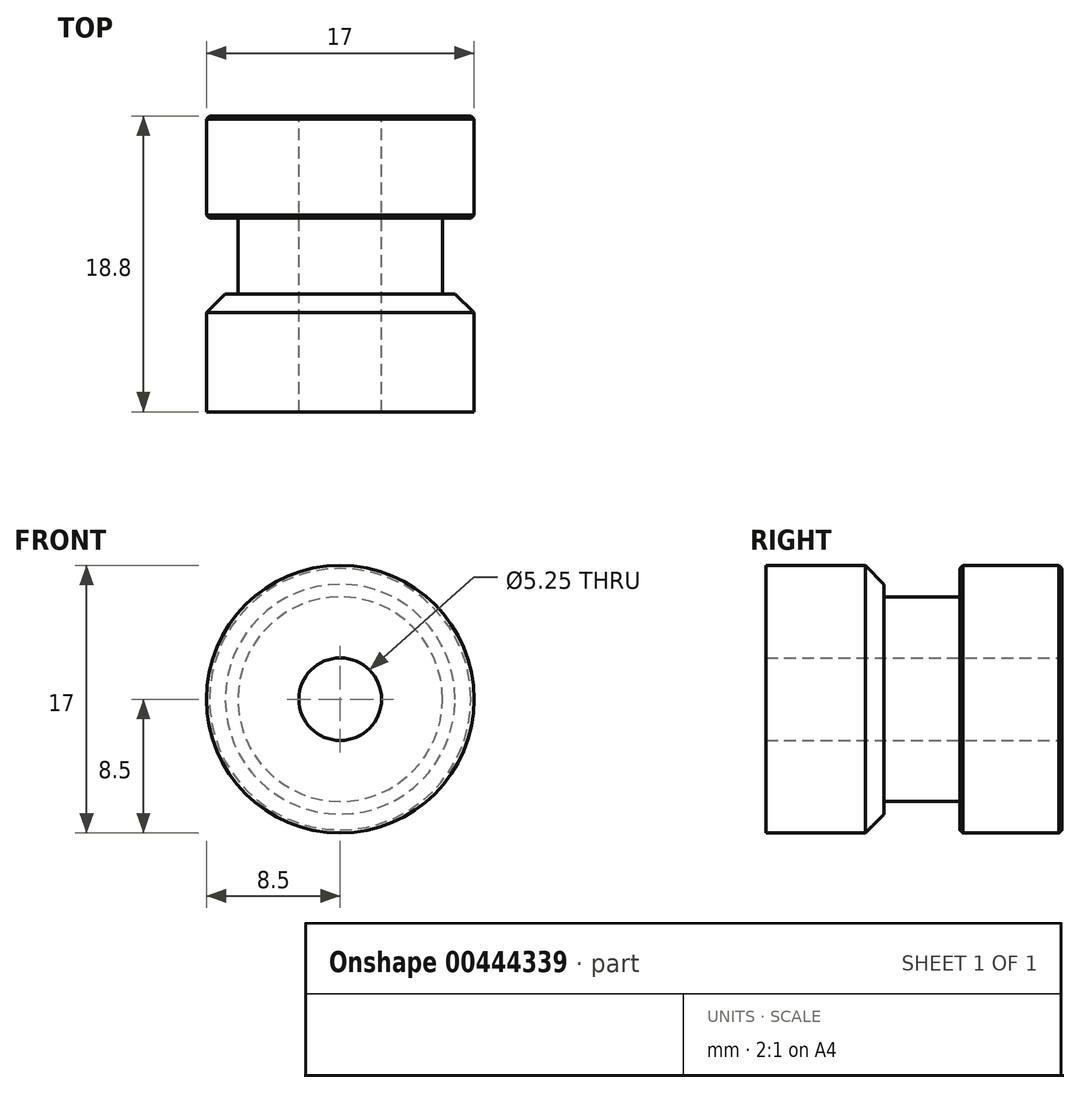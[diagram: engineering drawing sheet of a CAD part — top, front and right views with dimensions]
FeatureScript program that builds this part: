
annotation { "Feature Type Name" : "Feature", "Feature Type Description" : "" }
export const myFeature = defineFeature(function(context is Context, id is Id, definition is map)
    precondition{}
    {
        {
            var Q0;
            Q0=qCreatedBy(makeId("Front.planeOp"),FACE);
            var sketch = newSketch(context, id + "F0", { "sketchPlane" : qUnion([Q0])});
            skCircle(sketch, "E0", {"center": v(0, 0) * mm, "radius": 8.5 * mm});
            skCircle(sketch, "E1", {"center": v(0, 0) * mm, "radius": 2.63 * mm});
            skSolve(sketch);
        }
        {
            var Q0;
            Q0=makeQuery(id+"F0.imprint","IMPRINT",FACE,{"disambiguationData":[TD([[makeQuery(id+"F0.imprint","IMPRINT",EDGE,{"derivedFrom":sQuery(id+"F0.wireOp",EDGE,"E0")}),1.0]])]});
            extrude(context, id + "F1", {"entities" : qUnion([Q0]), "depth" : 6.5 * mm});
        }
        {
            var Q0;
            Q0=makeQuery(id+"F1.opExtrude","CAP_EDGE",EDGE,{"disambiguationData":[OSD([sQuery(id+"F0.wireOp",EDGE,"E0")])],"isStart":true});
            chamfer(context, id + "F2", {"entities" : qUnion([Q0]), "width" : 0.2 * mm, "tangentPropagation" : true});
        }
        {
            var Q0;
            Q0=makeQuery(id+"F1.opExtrude","CAP_FACE",FACE,{"disambiguationData":[OSD([sQuery(id+"F0.wireOp",EDGE,"E0"),sQuery(id+"F0.wireOp",EDGE,"E1")])],"isStart":false});
            var sketch = newSketch(context, id + "F3", { "sketchPlane" : qUnion([Q0])});
            skCircle(sketch, "E2", {"center": v(0, 0) * mm, "radius": 6.5 * mm});
            skCircle(sketch, "E3", {"center": v(0, 0) * mm, "radius": 2.62 * mm});
            skSolve(sketch);
        }
        {
            var Q0;
            Q0=makeQuery(id+"F3.imprint","IMPRINT",FACE,{"disambiguationData":[TD([[makeQuery(id+"F3.imprint","IMPRINT",EDGE,{"derivedFrom":sQuery(id+"F3.wireOp",EDGE,"E2")}),1.0]])]});
            extrude(context, id + "F4", {"entities" : qUnion([Q0]), "operationType" : NewBodyOperationType.ADD, "depth" : 4.8 * mm});
        }
        {
            var Q0;
            Q0=makeQuery(id+"F4.opExtrude","CAP_FACE",FACE,{"disambiguationData":[OSD([sQuery(id+"F0.wireOp",EDGE,"E1"),sQuery(id+"F3.wireOp",EDGE,"E2")])],"isStart":false});
            var sketch = newSketch(context, id + "F5", { "sketchPlane" : qUnion([Q0])});
            skCircle(sketch, "E4", {"center": v(0, 0) * mm, "radius": 2.62 * mm});
            skCircle(sketch, "E5", {"center": v(0, 0) * mm, "radius": 8.5 * mm});
            skSolve(sketch);
        }
        {
            var Q0;
            Q0 = qSketchRegion(id + "F5", true);
            extrude(context, id + "F6", {"entities" : qUnion([Q0]), "operationType" : NewBodyOperationType.ADD, "depth" : 7.5 * mm});
        }
        {
            var Q0;
            Q0=makeQuery(id+"F6.opExtrude","CAP_EDGE",EDGE,{"disambiguationData":[OSD([sQuery(id+"F5.wireOp",EDGE,"E5")])],"isStart":true});
            chamfer(context, id + "F7", {"entities" : qUnion([Q0]), "width" : 1.2 * mm, "tangentPropagation" : true});
        }
        {
            var Q0;
            Q0=makeQuery(id+"F1.opExtrude","CAP_EDGE",EDGE,{"disambiguationData":[OSD([sQuery(id+"F0.wireOp",EDGE,"E0")])],"isStart":false});
            chamfer(context, id + "F8", {"entities" : qUnion([Q0]), "width" : 0.2 * mm, "tangentPropagation" : true});
        }
    });
